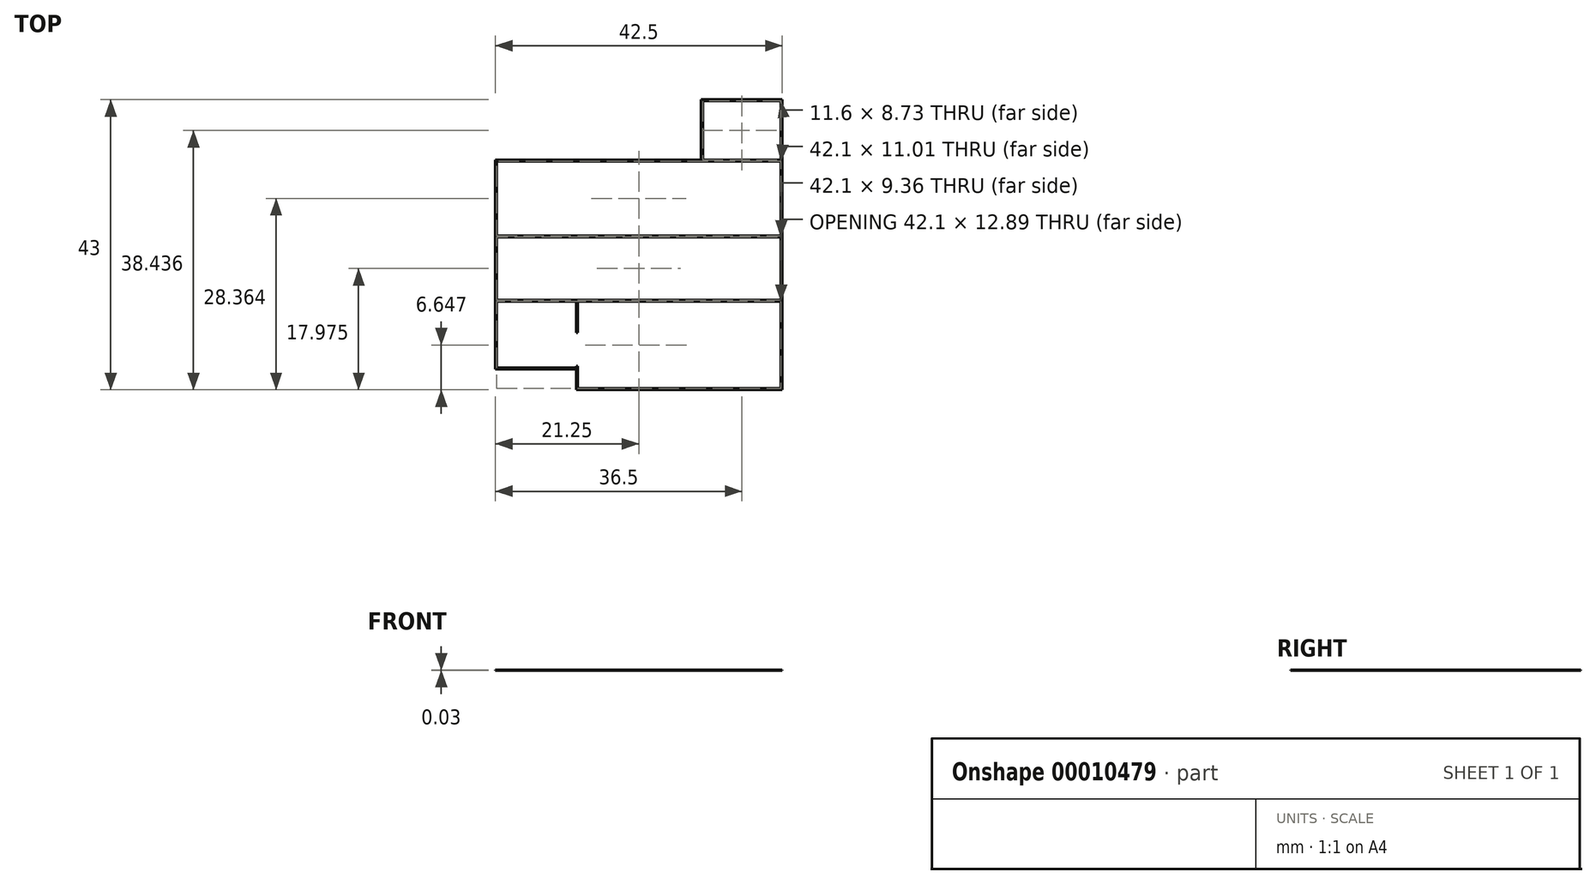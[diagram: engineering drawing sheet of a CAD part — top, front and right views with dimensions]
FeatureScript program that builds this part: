
annotation { "Feature Type Name" : "Feature", "Feature Type Description" : "" }
export const myFeature = defineFeature(function(context is Context, id is Id, definition is map)
    precondition{}
    {
        {
            var Q0;
            Q0=qCreatedBy(makeId("Top.planeOp"),FACE);
            var sketch = newSketch(context, id + "F0", { "sketchPlane" : qUnion([Q0])});
            skLineSegment(sketch, "E0.bottom", {"start": v(-42.5, 34.07) * mm, "end": v(-12, 34.07) * mm});
            skLineSegment(sketch, "E0.top", {"start": v(-42.3, 13.1) * mm, "end": v(-30.5, 13.1) * mm});
            skLineSegment(sketch, "E1", {"start": v(-42.5, 34.07) * mm, "end": v(-42.5, 3.07) * mm});
            skLineSegment(sketch, "E2", {"start": v(-42.5, 3.07) * mm, "end": v(-30.5, 3.07) * mm});
            skLineSegment(sketch, "E3", {"start": v(-30.5, 13.1) * mm, "end": v(-30.5, 8.5) * mm});
            skLineSegment(sketch, "E4", {"start": v(-30.5, 0) * mm, "end": v(0, 0) * mm});
            skLineSegment(sketch, "E5", {"start": v(0, 0) * mm, "end": v(0, 43) * mm});
            skLineSegment(sketch, "E6", {"start": v(0, 43) * mm, "end": v(-12, 43) * mm});
            skLineSegment(sketch, "E7", {"start": v(-12, 43) * mm, "end": v(-12, 34.07) * mm});
            skLineSegment(sketch, "E8.bottom", {"start": v(-11.8, 42.8) * mm, "end": v(-0.2, 42.8) * mm});
            skLineSegment(sketch, "E8.top", {"start": v(-11.8, 34.07) * mm, "end": v(-0.2, 34.07) * mm});
            skLineSegment(sketch, "E8.left", {"start": v(-11.8, 42.8) * mm, "end": v(-11.8, 34.07) * mm});
            skLineSegment(sketch, "E8.right", {"start": v(-0.2, 42.8) * mm, "end": v(-0.2, 34.07) * mm});
            skLineSegment(sketch, "E9.bottom", {"start": v(-0.2, 22.86) * mm, "end": v(-42.3, 22.86) * mm});
            skLineSegment(sketch, "E9.top", {"start": v(-0.2, 33.87) * mm, "end": v(-42.3, 33.87) * mm});
            skLineSegment(sketch, "E9.left", {"start": v(-0.2, 22.86) * mm, "end": v(-0.2, 33.87) * mm});
            skLineSegment(sketch, "E9.right", {"start": v(-42.3, 22.86) * mm, "end": v(-42.3, 33.87) * mm});
            skLineSegment(sketch, "E10.bottom", {"start": v(-42.3, 22.66) * mm, "end": v(-0.2, 22.66) * mm});
            skLineSegment(sketch, "E10.top", {"start": v(-42.3, 13.3) * mm, "end": v(-0.2, 13.3) * mm});
            skLineSegment(sketch, "E10.left", {"start": v(-42.3, 22.66) * mm, "end": v(-42.3, 13.3) * mm});
            skLineSegment(sketch, "E10.right", {"start": v(-0.2, 22.66) * mm, "end": v(-0.2, 13.3) * mm});
            skLineSegment(sketch, "E11", {"start": v(-42.3, 13.1) * mm, "end": v(-42.3, 3.27) * mm});
            skLineSegment(sketch, "E12", {"start": v(-42.3, 3.27) * mm, "end": v(-30.5, 3.27) * mm});
            skLineSegment(sketch, "E13", {"start": v(-30.3, 0.2) * mm, "end": v(-0.2, 0.2) * mm});
            skLineSegment(sketch, "E14", {"start": v(-0.2, 13.1) * mm, "end": v(-0.2, 0.2) * mm});
            skLineSegment(sketch, "E15.trimOffspring", {"start": v(-30.5, 3.07) * mm, "end": v(-30.5, 0) * mm});
            skLineSegment(sketch, "E16", {"start": v(-30.3, 0.2) * mm, "end": v(-30.3, 3.5) * mm});
            skLineSegment(sketch, "E17.trimOffspring", {"start": v(-30.3, 13.1) * mm, "end": v(-0.2, 13.1) * mm});
            skLineSegment(sketch, "E18", {"start": v(-30.5, 3.5) * mm, "end": v(-30.3, 3.5) * mm});
            skLineSegment(sketch, "E19", {"start": v(-30.5, 8.5) * mm, "end": v(-30.3, 8.5) * mm});
            skLineSegment(sketch, "E20.trimOffspring", {"start": v(-30.3, 8.5) * mm, "end": v(-30.3, 13.1) * mm});
            skLineSegment(sketch, "E21.trimOffspring", {"start": v(-30.5, 3.5) * mm, "end": v(-30.5, 3.27) * mm});
            skSolve(sketch);
        }
        {
            var Q0;
            Q0 = qSketchRegion(id + "F0", true);
            extrude(context, id + "F1", {"entities" : qUnion([Q0]), "depth" : 0.03 * mm});
        }
    });
